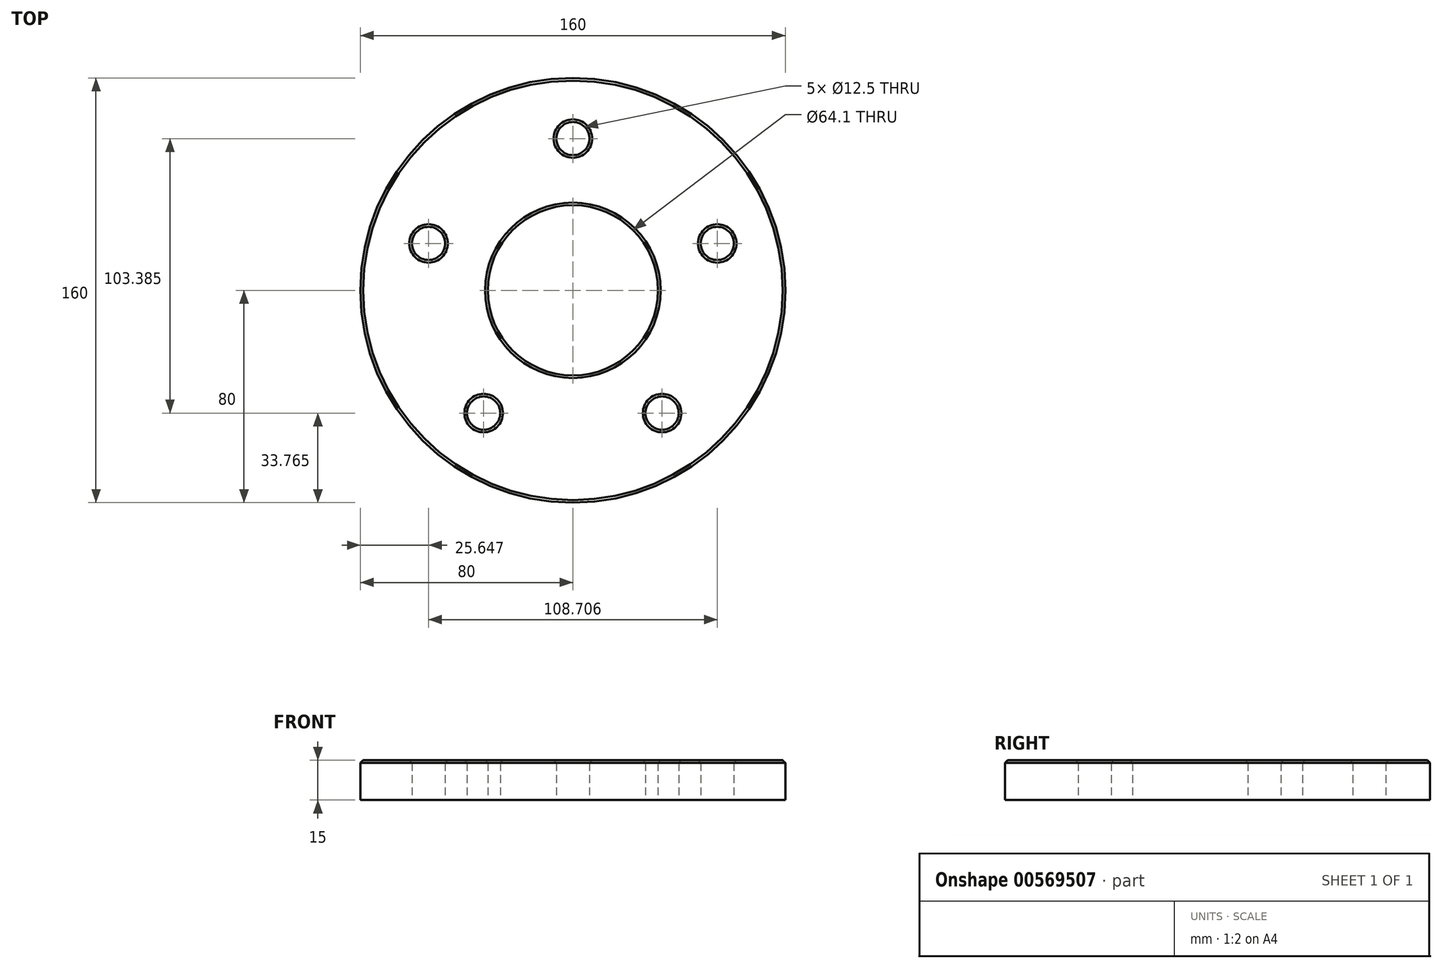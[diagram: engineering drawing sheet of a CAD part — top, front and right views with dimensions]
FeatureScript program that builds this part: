
annotation { "Feature Type Name" : "Feature", "Feature Type Description" : "" }
export const myFeature = defineFeature(function(context is Context, id is Id, definition is map)
    precondition{}
    {
        {
            var Q0;
            Q0=qCreatedBy(makeId("Top.planeOp"),FACE);
            var sketch = newSketch(context, id + "F0", { "sketchPlane" : qUnion([Q0])});
            skCircle(sketch, "E0", {"center": v(0, 0) * mm, "radius": 32.05 * mm});
            skCircle(sketch, "E1", {"center": v(0, 0) * mm, "radius": 57.15 * mm, "construction": true});
            skCircle(sketch, "E2", {"center": v(0, 57.15) * mm, "radius": 6.25 * mm});
            skCircle(sketch, "E3.1.0", {"center": v(-54.35, 17.66) * mm, "radius": 6.25 * mm});
            skCircle(sketch, "E3.2.0", {"center": v(-33.6, -46.24) * mm, "radius": 6.25 * mm});
            skCircle(sketch, "E3.3.0", {"center": v(33.6, -46.24) * mm, "radius": 6.25 * mm});
            skCircle(sketch, "E3.4.0", {"center": v(54.35, 17.66) * mm, "radius": 6.25 * mm});
            skCircle(sketch, "E4", {"center": v(0, 0) * mm, "radius": 80 * mm});
            skSolve(sketch);
        }
        {
            var Q0;
            Q0=makeQuery(id+"F0.imprint","IMPRINT",FACE,{"disambiguationData":[TD([[makeQuery(id+"F0.imprint","IMPRINT",EDGE,{"derivedFrom":sQuery(id+"F0.wireOp",EDGE,"E0")}),-1.0]])]});
            extrude(context, id + "F1", {"entities" : qUnion([Q0]), "depth" : 15 * mm, "offsetDistance" : 25 * mm});
        }
        {
            var Q0;
            Q0=makeQuery(id+"F1.opExtrude","CAP_FACE",FACE,{"disambiguationData":[OSD([sQuery(id+"F0.wireOp",EDGE,"E0"),sQuery(id+"F0.wireOp",EDGE,"E2"),sQuery(id+"F0.wireOp",EDGE,"E3.1.0"),sQuery(id+"F0.wireOp",EDGE,"E3.2.0"),sQuery(id+"F0.wireOp",EDGE,"E3.3.0"),sQuery(id+"F0.wireOp",EDGE,"E3.4.0"),sQuery(id+"F0.wireOp",EDGE,"E4")])],"isStart":false});
            chamfer(context, id + "F2", {"entities" : qUnion([Q0]), "width" : 1 * mm, "tangentPropagation" : true});
        }
    });
